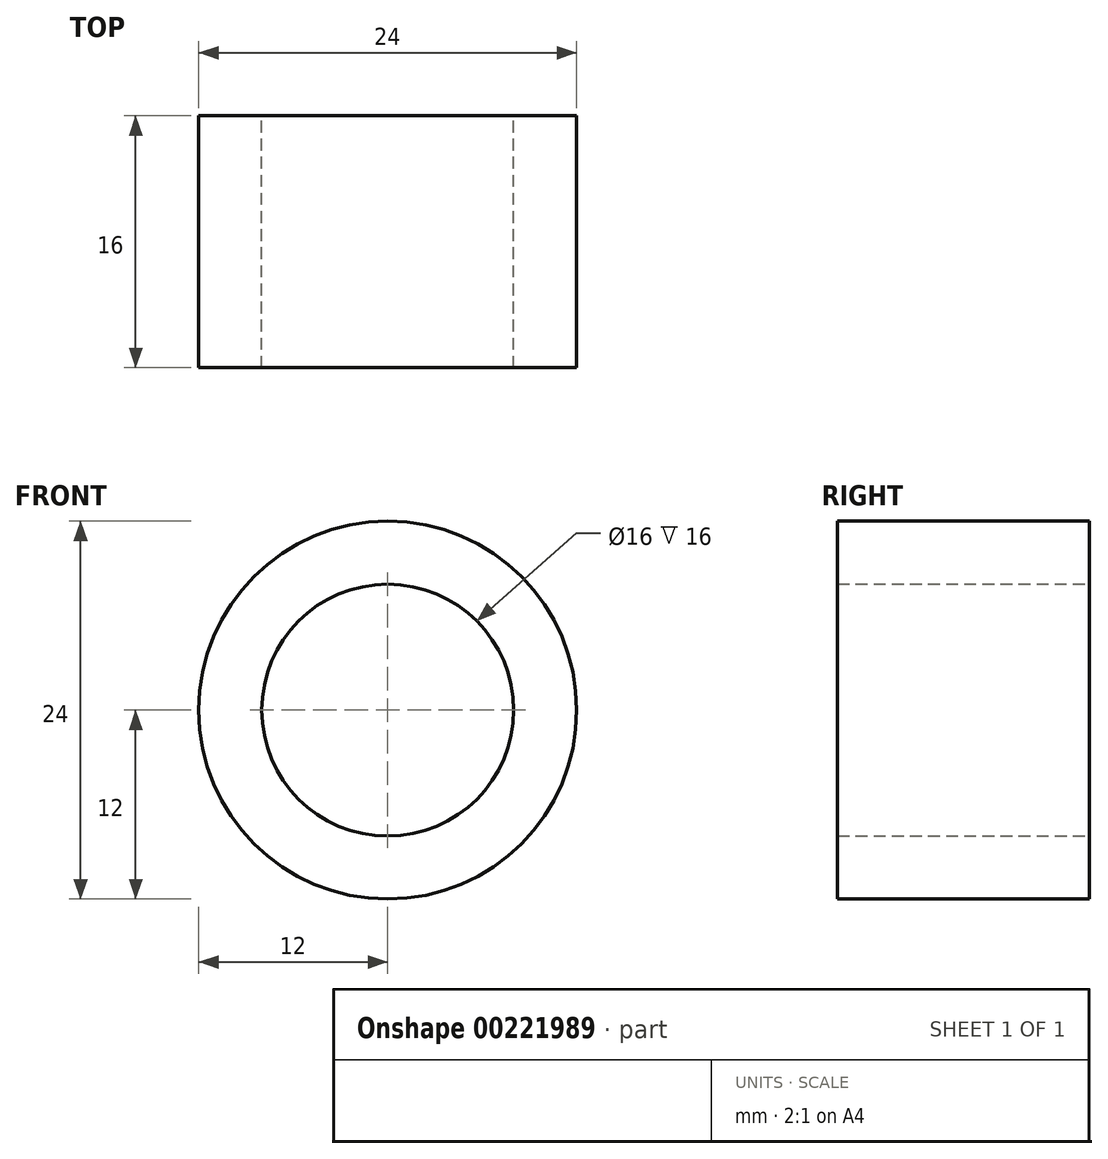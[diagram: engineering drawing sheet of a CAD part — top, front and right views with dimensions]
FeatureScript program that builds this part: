
annotation { "Feature Type Name" : "Feature", "Feature Type Description" : "" }
export const myFeature = defineFeature(function(context is Context, id is Id, definition is map)
    precondition{}
    {
        {
            var Q0;
            Q0=qCreatedBy(makeId("Front.planeOp"),FACE);
            var sketch = newSketch(context, id + "F0", { "sketchPlane" : qUnion([Q0])});
            skCircle(sketch, "E0", {"center": v(0, 0) * mm, "radius": 8 * mm});
            skCircle(sketch, "E1", {"center": v(0, 0) * mm, "radius": 12 * mm});
            skSolve(sketch);
        }
        {
            var Q0;
            Q0 = qSketchRegion(id + "F0", true);
            extrude(context, id + "F1", {"entities" : qUnion([Q0]), "depth" : 16 * mm});
        }
    });
